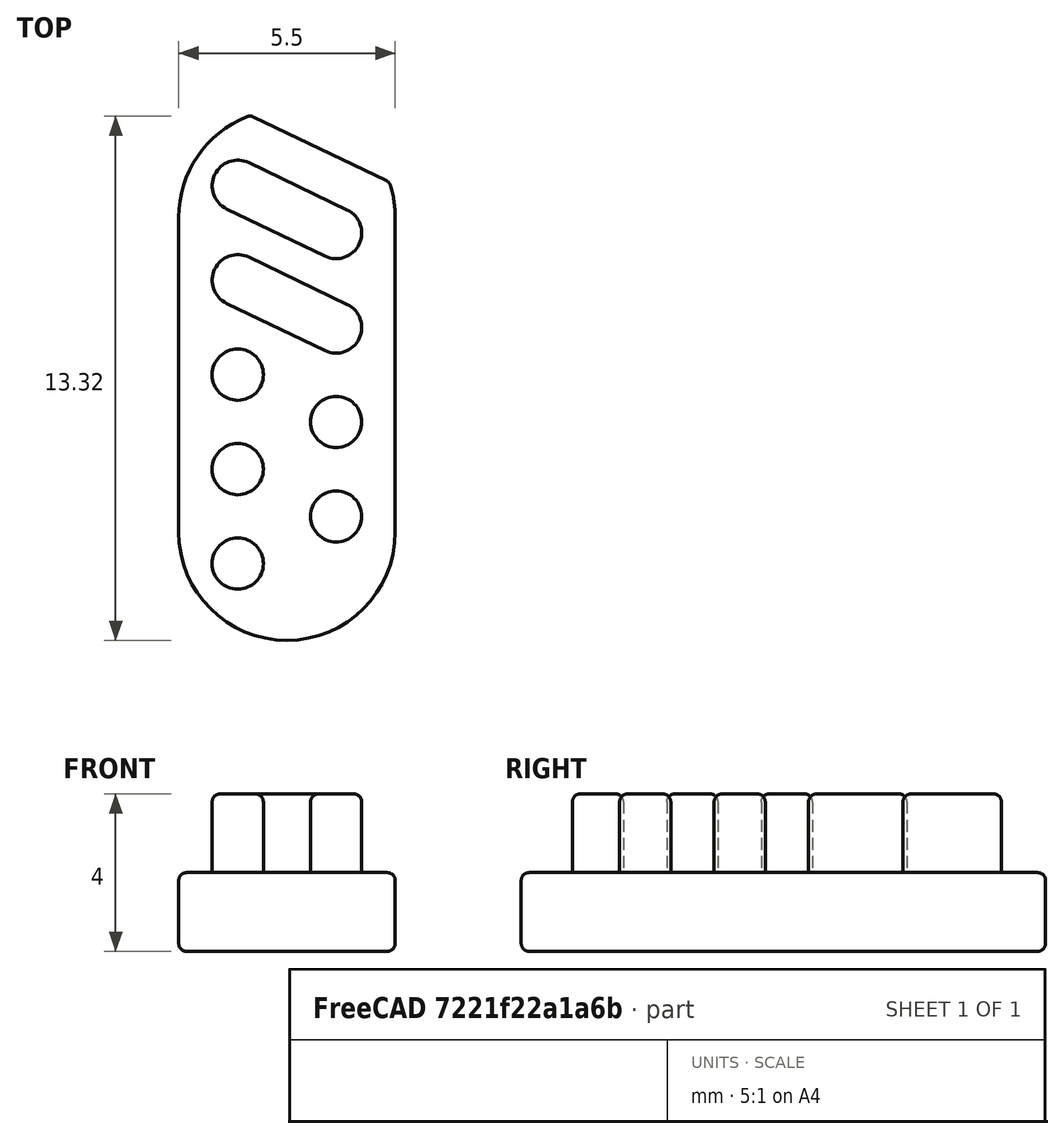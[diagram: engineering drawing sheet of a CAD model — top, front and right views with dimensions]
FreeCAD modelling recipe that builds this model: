
FCSTD DOCUMENT  (FreeCAD 0.18R13959 (Git))
Label: Light_Diffuser-PCB-v1.7
License: CreativeCommons Attribution-NonCommercial-ShareAlike
LicenseURL: http://creativecommons.org/licenses/by-nc-sa/4.0/
objects: Sketcher::SketchObject×3, PartDesign::Pad×2, PartDesign::Fillet×2, PartDesign::Body×1, Mesh::Feature×1
note: 10 computed .brp shape members not serialized (recipe doc carries the construction recipe); baked Part::Feature solids carry a one-line shape summary decoded from their .brp

FEATURE [Sketcher::SketchObject] Sketch
  MapMode = 5
  Support = -> [XY_Plane]
FEATURE [Sketcher::SketchObject] Sketch009
  MapMode = 5
  Placement = pos=(0,0,15.5) rot=(0,0,1;0rad)
  sketch-geometry (47):
    g0: LineSegment [constr] StartX=26.0494 StartY=8.19084 StartZ=0 EndX=28.5494 EndY=8.19084 EndZ=0
    g1: LineSegment [constr] StartX=28.5494 StartY=8.19084 StartZ=0 EndX=28.5494 EndY=-1.40916 EndZ=0
    g2: LineSegment [constr] StartX=28.5494 StartY=-1.40916 StartZ=0 EndX=26.0494 EndY=-1.40916 EndZ=0
    g3: LineSegment [constr] StartX=26.0494 StartY=-1.40916 StartZ=0 EndX=26.0494 EndY=8.19084 EndZ=0
    g4: LineSegment [constr] StartX=26.0494 StartY=6.99084 StartZ=0 EndX=28.5494 EndY=6.99084 EndZ=0
    g5: LineSegment [constr] StartX=26.0494 StartY=5.79084 StartZ=0 EndX=28.5494 EndY=5.79084 EndZ=0
    g6: LineSegment [constr] StartX=26.0494 StartY=4.59084 StartZ=0 EndX=28.5494 EndY=4.59084 EndZ=0
    g7: LineSegment [constr] StartX=26.0494 StartY=3.39084 StartZ=0 EndX=28.5494 EndY=3.39084 EndZ=0
    g8: LineSegment [constr] StartX=26.0494 StartY=2.19084 StartZ=0 EndX=28.5494 EndY=2.19084 EndZ=0
    g9: LineSegment [constr] StartX=26.0494 StartY=0.990836 StartZ=0 EndX=28.5494 EndY=0.990836 EndZ=0
    g10: LineSegment [constr] StartX=26.0494 StartY=-0.209164 StartZ=0 EndX=28.5494 EndY=-0.209164 EndZ=0
    g11: ArcOfCircle [constr] CenterX=26.0494 CenterY=8.19084 CenterZ=0 NormalX=0 NormalY=0 NormalZ=1 AngleXU=0 Radius=0.75 StartAngle=1.12328 EndAngle=4.26487
    g12: ArcOfCircle [constr] CenterX=28.5494 CenterY=6.99084 CenterZ=0 NormalX=0 NormalY=0 NormalZ=1 AngleXU=0 Radius=0.75 StartAngle=4.26487 EndAngle=7.40646
    g13: Circle [constr] CenterX=28.5494 CenterY=6.99084 CenterZ=0 NormalX=0 NormalY=0 NormalZ=1 AngleXU=0 Radius=0.75
    g14: Circle [constr] CenterX=26.0494 CenterY=8.19084 CenterZ=0 NormalX=0 NormalY=0 NormalZ=1 AngleXU=0 Radius=0.75
    g15: LineSegment [constr] StartX=25.5171 StartY=9.27827 StartZ=0 EndX=28.8383 EndY=7.68412 EndZ=0
    g16: LineSegment [constr] StartX=24.3258 StartY=8.18624 StartZ=0 EndX=27.642 EndY=6.59448 EndZ=0
    g17: LineSegment [constr] StartX=26.374 StartY=8.86698 StartZ=0 EndX=28.874 EndY=7.66698 EndZ=0
    g18: LineSegment [constr] StartX=25.7249 StartY=7.51469 StartZ=0 EndX=28.2249 EndY=6.31469 EndZ=0
    g19: ArcOfCircle [constr] CenterX=26.0494 CenterY=5.79084 CenterZ=0 NormalX=0 NormalY=0 NormalZ=1 AngleXU=0 Radius=0.75 StartAngle=1.34506 EndAngle=4.05341
    g20: LineSegment [constr] StartX=26.2173 StartY=6.52181 StartZ=0 EndX=28.7014 EndY=5.32527 EndZ=0
    g21: ArcOfCircle [constr] CenterX=28.5494 CenterY=4.59084 CenterZ=0 NormalX=0 NormalY=0 NormalZ=1 AngleXU=0 Radius=0.75 StartAngle=4.03537 EndAngle=7.64991
    g22: LineSegment [constr] StartX=25.5902 StartY=5.19787 StartZ=0 EndX=28.0796 EndY=4.00625 EndZ=0
    g23: Circle [constr] CenterX=26.0494 CenterY=-1.40916 CenterZ=0 NormalX=0 NormalY=0 NormalZ=1 AngleXU=0 Radius=0.75
    g24: Circle [constr] CenterX=28.5494 CenterY=-0.209164 CenterZ=0 NormalX=0 NormalY=0 NormalZ=1 AngleXU=0 Radius=0.75
    g25: Circle [constr] CenterX=26.0494 CenterY=0.990836 CenterZ=0 NormalX=0 NormalY=0 NormalZ=1 AngleXU=0 Radius=0.75
    g26: Circle [constr] CenterX=28.5494 CenterY=2.19084 CenterZ=0 NormalX=0 NormalY=0 NormalZ=1 AngleXU=0 Radius=0.75
    g27: Circle [constr] CenterX=26.0494 CenterY=3.39084 CenterZ=0 NormalX=0 NormalY=0 NormalZ=1 AngleXU=0 Radius=0.75
    g28: LineSegment [constr] StartX=25.99 StartY=-2.26963 StartZ=0 EndX=28.2803 EndY=-1.17028 EndZ=0
    g29: LineSegment [constr] StartX=24.2621 StartY=-1.43517 StartZ=0 EndX=27.5897 EndY=0.162095 EndZ=0
    g30: LineSegment [constr] StartX=24.4431 StartY=0.929921 StartZ=0 EndX=28.3215 EndY=-0.931678 EndZ=0
    g31: LineSegment [constr] StartX=25.7479 StartY=1.96747 StartZ=0 EndX=28.6552 EndY=0.57196 EndZ=0
    g32: LineSegment [constr] StartX=25.0985 StartY=-0.297502 StartZ=0 EndX=28.7983 EndY=1.4784 EndZ=0
    g33: LineSegment [constr] StartX=24.2499 StartY=0.959014 StartZ=0 EndX=27.3959 EndY=2.46909 EndZ=0
    g34: LineSegment [constr] StartX=24.4539 StartY=3.32474 StartZ=0 EndX=27.6201 EndY=1.80499 EndZ=0
    g35: Circle [constr] CenterX=26.0494 CenterY=2.19084 CenterZ=0 NormalX=0 NormalY=0 NormalZ=1 AngleXU=0 Radius=0.331828
    g36: Circle [constr] CenterX=28.5494 CenterY=0.990836 CenterZ=0 NormalX=0 NormalY=0 NormalZ=1 AngleXU=0 Radius=0.331828
    g37: Circle [constr] CenterX=26.0494 CenterY=-0.209164 CenterZ=0 NormalX=0 NormalY=0 NormalZ=1 AngleXU=0 Radius=0.331828
    g38: LineSegment [constr] StartX=27.2994 StartY=10.3721 StartZ=0 EndX=27.2994 EndY=-2.82328 EndZ=0
    g39: ArcOfCircle [constr] CenterX=27.2994 CenterY=7.39084 CenterZ=0 NormalX=0 NormalY=0 NormalZ=1 AngleXU=0 Radius=2.75 StartAngle=0 EndAngle=3.14159
    g40: ArcOfCircle CenterX=27.2994 CenterY=-0.609164 CenterZ=0 NormalX=0 NormalY=0 NormalZ=1 AngleXU=0 Radius=2.75 StartAngle=3.14159 EndAngle=6.28319
    g41: LineSegment StartX=24.5494 StartY=7.39084 StartZ=0 EndX=24.5494 EndY=-0.609164 EndZ=0
    g42: LineSegment StartX=30.0494 StartY=7.39084 StartZ=0 EndX=30.0494 EndY=-0.609164 EndZ=0
    g43: LineSegment [constr] StartX=24.5693 StartY=10.8425 StartZ=0 EndX=31.1469 EndY=7.68522 EndZ=0
    g44: ArcOfCircle CenterX=27.2994 CenterY=7.39084 CenterZ=0 NormalX=0 NormalY=0 NormalZ=1 AngleXU=0 Radius=2.75 StartAngle=1.91597 EndAngle=3.14159
    g45: ArcOfCircle CenterX=27.2994 CenterY=7.39084 CenterZ=0 NormalX=0 NormalY=0 NormalZ=1 AngleXU=0 Radius=2.75 StartAngle=0 EndAngle=0.330582
    g46: LineSegment StartX=26.3689 StartY=9.97863 StartZ=0 EndX=29.9005 EndY=8.28347 EndZ=0
  constraints (117):
    c: Coincident(g0,g1)
    c: Coincident(g1,g2)
    c: Coincident(g2,g3)
    c: Coincident(g3,g0)
    c: Horizontal(g0)
    c: Horizontal(g2)
    c: Vertical(g1)
    c: Vertical(g3)
    c: DistanceX(g0,g0) = 2.5
    c: DistanceY(g3,g3) = 9.6
    c: Horizontal(g4)
    c: Horizontal(g5)
    c: Horizontal(g6)
    c: Horizontal(g8)
    c: Horizontal(g9)
    c: DistanceY(g4,g0) = 1.2
    c: DistanceY(g5,g4) = 1.2
    c: DistanceY(g6,g5) = 1.2
    c: DistanceY(g7,g6) = 1.2
    c: DistanceY(g8,g7) = 1.2
    c: DistanceY(g9,g8) = 1.2
    c: Horizontal(g10)
    c: DistanceY(g10,g9) = 1.2
    c: PointOnObject(g4,g3)
    c: PointOnObject(g5,g3)
    c: PointOnObject(g6,g3)
    c: PointOnObject(g7,g3)
    c: PointOnObject(g8,g3)
    c: PointOnObject(g9,g3)
    c: PointOnObject(g10,g3)
    c: PointOnObject(g10,g1)
    c: PointOnObject(g9,g1)
    c: PointOnObject(g8,g1)
    c: PointOnObject(g7,g1)
    c: PointOnObject(g6,g1)
    c: PointOnObject(g5,g1)
    c: PointOnObject(g4,g1)
    c: Coincident(g11,g0)
    c: Coincident(g12,g4)
    c: Radius(g11) = 0.75
    c: Radius(g12) = 0.75
    c: Coincident(g13,g4)
    c: Coincident(g14,g0)
    c: Radius(g14) = 0.75
    c: Radius(g13) = 0.75
    c: Tangent(g15,g13)
    c: Tangent(g15,g14)
    c: Tangent(g16,g14)
    c: Tangent(g16,g13)
    c: PointOnObject(g17,g15)
    c: PointOnObject(g17,g15)
    c: PointOnObject(g18,g16)
    c: PointOnObject(g18,g16)
    c: Coincident(g17,g11)
    c: Coincident(g11,g18)
    c: Coincident(g17,g12)
    c: Coincident(g12,g18)
    c: Equal(g11,g19) = 0.75
    c: Equal(g12,g21) = 0.75
    c: Coincident(g20,g19)
    c: Coincident(g19,g22)
    c: Coincident(g20,g21)
    c: Coincident(g21,g22)
    c: Coincident(g19,g5)
    c: Coincident(g21,g6)
    c: Coincident(g24,g10)
    c: Coincident(g25,g9)
    c: Coincident(g26,g8)
    c: Coincident(g27,g7)
    c: Radius(g27) = 0.75
    c: Radius(g26) = 0.75
    c: Radius(g25) = 0.75
    c: Radius(g24) = 0.75
    c: Radius(g23) = 0.75
    c: Tangent(g31,g24)
    c: Tangent(g31,g25)
    c: Tangent(g30,g25)
    c: Tangent(g30,g24)
    c: Tangent(g29,g23)
    c: Tangent(g29,g24)
    c: Coincident(g23,g2)
    c: Tangent(g23,g28)
    c: Tangent(g28,g24)
    c: Tangent(g32,g25)
    c: Tangent(g32,g26)
    c: Tangent(g33,g26)
    c: Tangent(g33,g25)
    c: Tangent(g34,g27)
    c: Tangent(g34,g26)
    c: Coincident(g35,g8)
    c: Tangent(g35,g34)
    c: Coincident(g36,g9)
    c: Tangent(g36,g32)
    c: Coincident(g37,g10)
    c: Tangent(g37,g30)
    c: Vertical(g38)
    c: Symmetric(g0,g0,g38)
    c: Tangent(g39,g42)
    c: Tangent(g39,g41)
    c: Tangent(g41,g40)
    c: Tangent(g42,g40)
    c: Vertical(g41)
    c: Equal(g39,g40)
    c: PointOnObject(g39,g38)
    c: DistanceY(g40,g39) = 8
    c: Symmetric(g40,g39,g7)
    c: DistanceX(g40,g40) = 5.5
    c: Parallel(g43,g15)
    c: Coincident(g44,g39)
    c: Coincident(g44,g39)
    c: Coincident(g45,g39)
    c: Coincident(g45,g39)
    c: Distance(g15,g43) = 1
    c: PointOnObject(g46,g43)
    c: PointOnObject(g46,g43)
    c: Coincident(g45,g46)
    c: Coincident(g44,g46)
FEATURE [PartDesign::Pad] Pad
  Length = 2
  Length2 = 100
  Placement = pos=(0,0,15.5) rot=(0,0,1;0rad)
  Profile = -> Sketch009
  Type = 0
FEATURE [Sketcher::SketchObject] Sketch010
  ExternalGeometry = -> [Pad]
  MapMode = 5
  Placement = pos=(0,0,17.5) rot=(0,0,1;0rad)
  Support = -> [Pad]
  expr: Constraints[39] = Sketch009.Constraints[43]
  expr: Constraints[8] = Sketch009.Constraints[8]
  expr: Constraints[40] = Sketch009.Constraints[44]
  expr: Constraints[56] = Sketch009.Constraints[72]
  expr: Constraints[57] = Sketch009.Constraints[73]
  expr: Constraints[15] = Sketch009.Constraints[15]
  expr: Constraints[55] = Sketch009.Constraints[71]
  expr: Constraints[53] = Sketch009.Constraints[69]
  expr: Constraints[9] = Sketch009.Constraints[9]
  expr: Constraints[54] = Sketch009.Constraints[70]
  expr: Constraints[17] = Sketch009.Constraints[17]
  expr: Constraints[19] = Sketch009.Constraints[19]
  expr: Constraints[18] = Sketch009.Constraints[18]
  expr: Constraints[16] = Sketch009.Constraints[16]
  expr: Constraints[20] = Sketch009.Constraints[20]
  expr: Constraints[22] = Sketch009.Constraints[22]
  sketch-geometry (60):
    g0: LineSegment [constr] StartX=26.0494 StartY=8.19084 StartZ=0 EndX=28.5494 EndY=8.19084 EndZ=0
    g1: LineSegment [constr] StartX=28.5494 StartY=8.19084 StartZ=0 EndX=28.5494 EndY=-1.40916 EndZ=0
    g2: LineSegment [constr] StartX=28.5494 StartY=-1.40916 StartZ=0 EndX=26.0494 EndY=-1.40916 EndZ=0
    g3: LineSegment [constr] StartX=26.0494 StartY=-1.40916 StartZ=0 EndX=26.0494 EndY=8.19084 EndZ=0
    g4: LineSegment [constr] StartX=26.0494 StartY=6.99084 StartZ=0 EndX=28.5494 EndY=6.99084 EndZ=0
    g5: LineSegment [constr] StartX=26.0494 StartY=5.79084 StartZ=0 EndX=28.5494 EndY=5.79084 EndZ=0
    g6: LineSegment [constr] StartX=26.0494 StartY=4.59084 StartZ=0 EndX=28.5494 EndY=4.59084 EndZ=0
    g7: LineSegment [constr] StartX=26.0494 StartY=3.39084 StartZ=0 EndX=28.5494 EndY=3.39084 EndZ=0
    g8: LineSegment [constr] StartX=26.0494 StartY=2.19084 StartZ=0 EndX=28.5494 EndY=2.19084 EndZ=0
    g9: LineSegment [constr] StartX=26.0494 StartY=0.990836 StartZ=0 EndX=28.5494 EndY=0.990836 EndZ=0
    g10: LineSegment [constr] StartX=26.0494 StartY=-0.209164 StartZ=0 EndX=28.5494 EndY=-0.209164 EndZ=0
    g11: Circle [constr] CenterX=28.5494 CenterY=6.99084 CenterZ=0 NormalX=0 NormalY=0 NormalZ=1 AngleXU=0 Radius=0.75
    g12: Circle [constr] CenterX=26.0494 CenterY=8.19084 CenterZ=0 NormalX=0 NormalY=0 NormalZ=1 AngleXU=0 Radius=0.75
    g13: LineSegment [constr] StartX=25.5635 StartY=9.25599 StartZ=0 EndX=28.8763 EndY=7.66586 EndZ=0
    g14: LineSegment [constr] StartX=24.3756 StartY=8.16234 StartZ=0 EndX=27.694 EndY=6.56949 EndZ=0
    g15: LineSegment [constr] StartX=25.798 StartY=9.14342 StartZ=0 EndX=28.298 EndY=7.94342 EndZ=0
    g16: LineSegment [constr] StartX=25.1489 StartY=7.79113 StartZ=0 EndX=27.6489 EndY=6.59113 EndZ=0
    g17: Circle [constr] CenterX=26.0494 CenterY=-1.40916 CenterZ=0 NormalX=0 NormalY=0 NormalZ=1 AngleXU=0 Radius=0.75
    g18: Circle [constr] CenterX=28.5494 CenterY=-0.209164 CenterZ=0 NormalX=0 NormalY=0 NormalZ=1 AngleXU=0 Radius=0.75
    g19: Circle [constr] CenterX=26.0494 CenterY=0.990836 CenterZ=0 NormalX=0 NormalY=0 NormalZ=1 AngleXU=0 Radius=0.75
    g20: Circle [constr] CenterX=28.5494 CenterY=2.19084 CenterZ=0 NormalX=0 NormalY=0 NormalZ=1 AngleXU=0 Radius=0.75
    g21: Circle [constr] CenterX=26.0494 CenterY=3.39084 CenterZ=0 NormalX=0 NormalY=0 NormalZ=1 AngleXU=0 Radius=0.75
    g22: LineSegment [constr] StartX=26.1522 StartY=-2.19175 StartZ=0 EndX=28.4416 EndY=-1.09284 EndZ=0
    g23: LineSegment [constr] StartX=24.424 StartY=-1.35742 StartZ=0 EndX=27.7513 EndY=0.239661 EndZ=0
    g24: LineSegment [constr] StartX=24.4948 StartY=0.905132 StartZ=0 EndX=28.3731 EndY=-0.956467 EndZ=0
    g25: LineSegment [constr] StartX=25.7996 StartY=1.94268 StartZ=0 EndX=28.7069 EndY=0.54717 EndZ=0
    g26: LineSegment [constr] StartX=25.26 StartY=-0.220018 StartZ=0 EndX=28.9598 EndY=1.55589 EndZ=0
    g27: LineSegment [constr] StartX=24.4114 StartY=1.0365 StartZ=0 EndX=27.5573 EndY=2.54657 EndZ=0
    g28: LineSegment [constr] StartX=24.5064 StartY=3.29957 StartZ=0 EndX=27.6722 EndY=1.77997 EndZ=0
    g29: Circle [constr] CenterX=26.0494 CenterY=2.19084 CenterZ=0 NormalX=0 NormalY=0 NormalZ=1 AngleXU=0 Radius=0.331828
    g30: Circle [constr] CenterX=28.5494 CenterY=0.990836 CenterZ=0 NormalX=0 NormalY=0 NormalZ=1 AngleXU=0 Radius=0.331828
    g31: Circle [constr] CenterX=26.0494 CenterY=-0.209164 CenterZ=0 NormalX=0 NormalY=0 NormalZ=1 AngleXU=0 Radius=0.331828
    g32: LineSegment [constr] StartX=27.2994 StartY=10.5023 StartZ=0 EndX=27.2994 EndY=-2.69309 EndZ=0
    g33: Circle [constr] CenterX=26.0494 CenterY=5.79084 CenterZ=0 NormalX=0 NormalY=0 NormalZ=1 AngleXU=0 Radius=0.75
    g34: Circle [constr] CenterX=28.5494 CenterY=4.59084 CenterZ=0 NormalX=0 NormalY=0 NormalZ=1 AngleXU=0 Radius=0.75
    g35: LineSegment [constr] StartX=25.2568 StartY=7.00319 StartZ=0 EndX=29.1124 EndY=5.15253 EndZ=0
    g36: LineSegment [constr] StartX=24.5022 StartY=5.70156 StartZ=0 EndX=28.1414 EndY=3.95476 EndZ=0
    g37: Circle CenterX=26.0494 CenterY=3.39084 CenterZ=0 NormalX=0 NormalY=0 NormalZ=1 AngleXU=0 Radius=0.65
    g38: Circle CenterX=28.5494 CenterY=2.19084 CenterZ=0 NormalX=0 NormalY=0 NormalZ=1 AngleXU=0 Radius=0.65
    g39: Circle CenterX=26.0494 CenterY=0.990836 CenterZ=0 NormalX=0 NormalY=0 NormalZ=1 AngleXU=0 Radius=0.65
    g40: Circle CenterX=26.0494 CenterY=-1.40916 CenterZ=0 NormalX=0 NormalY=0 NormalZ=1 AngleXU=0 Radius=0.65
    g41: Circle CenterX=28.5494 CenterY=-0.209164 CenterZ=0 NormalX=0 NormalY=0 NormalZ=1 AngleXU=0 Radius=0.65
    g42: Circle [constr] CenterX=28.5494 CenterY=6.99084 CenterZ=0 NormalX=0 NormalY=0 NormalZ=1 AngleXU=0 Radius=0.65
    g43: Circle [constr] CenterX=26.0494 CenterY=8.19084 CenterZ=0 NormalX=0 NormalY=0 NormalZ=1 AngleXU=0 Radius=0.65
    g44: LineSegment [constr] StartX=25.0896 StartY=9.37255 StartZ=0 EndX=28.8024 EndY=7.59041 EndZ=0
    g45: LineSegment [constr] StartX=24.3536 StartY=8.28381 StartZ=0 EndX=28.1684 EndY=6.45273 EndZ=0
    g46: Circle [constr] CenterX=26.0494 CenterY=5.79084 CenterZ=0 NormalX=0 NormalY=0 NormalZ=1 AngleXU=0 Radius=0.65
    g47: Circle [constr] CenterX=28.5494 CenterY=4.59084 CenterZ=0 NormalX=0 NormalY=0 NormalZ=1 AngleXU=0 Radius=0.65
    g48: LineSegment [constr] StartX=24.9879 StartY=7.02135 StartZ=0 EndX=28.8106 EndY=5.18647 EndZ=0
    g49: LineSegment [constr] StartX=24.6124 StartY=5.75959 StartZ=0 EndX=28.3692 EndY=3.95636 EndZ=0
    g50: ArcOfCircle CenterX=26.0494 CenterY=8.19084 CenterZ=0 NormalX=0 NormalY=0 NormalZ=1 AngleXU=0 Radius=0.65 StartAngle=1.12328 EndAngle=4.26488
    g51: ArcOfCircle CenterX=28.5494 CenterY=6.99084 CenterZ=0 NormalX=0 NormalY=0 NormalZ=1 AngleXU=0 Radius=0.65 StartAngle=4.26487 EndAngle=7.40646
    g52: ArcOfCircle CenterX=26.0494 CenterY=5.79084 CenterZ=0 NormalX=0 NormalY=0 NormalZ=1 AngleXU=0 Radius=0.65 StartAngle=1.12328 EndAngle=4.26487
    g53: ArcOfCircle CenterX=28.5494 CenterY=4.59084 CenterZ=0 NormalX=0 NormalY=0 NormalZ=1 AngleXU=0 Radius=0.65 StartAngle=4.26488 EndAngle=7.40646
    g54: LineSegment StartX=26.3307 StartY=8.77683 StartZ=0 EndX=28.8307 EndY=7.57683 EndZ=0
    g55: LineSegment StartX=25.7681 StartY=7.60484 StartZ=0 EndX=28.2681 EndY=6.40485 EndZ=0
    g56: LineSegment StartX=26.3307 StartY=6.37683 StartZ=0 EndX=28.8307 EndY=5.17683 EndZ=0
    g57: LineSegment StartX=25.7681 StartY=5.20485 StartZ=0 EndX=28.2681 EndY=4.00484 EndZ=0
    g58: LineSegment [constr] StartX=24.5494 StartY=7.20634 StartZ=0 EndX=24.5494 EndY=-0.230688 EndZ=0
    g59: LineSegment [constr] StartX=30.0494 StartY=7.20634 StartZ=0 EndX=30.0494 EndY=0.145812 EndZ=0
  constraints (146):
    c: Coincident(g0,g1)
    c: Coincident(g1,g2)
    c: Coincident(g2,g3)
    c: Coincident(g3,g0)
    c: Horizontal(g0)
    c: Horizontal(g2)
    c: Vertical(g1)
    c: Vertical(g3)
    c: DistanceX(g0,g0) = 2.5
    c: DistanceY(g3,g3) = 9.6
    c: Horizontal(g4)
    c: Horizontal(g5)
    c: Horizontal(g6)
    c: Horizontal(g8)
    c: Horizontal(g9)
    c: DistanceY(g4,g0) = 1.2
    c: DistanceY(g5,g4) = 1.2
    c: DistanceY(g6,g5) = 1.2
    c: DistanceY(g7,g6) = 1.2
    c: DistanceY(g8,g7) = 1.2
    c: DistanceY(g9,g8) = 1.2
    c: Horizontal(g10)
    c: DistanceY(g10,g9) = 1.2
    c: PointOnObject(g4,g3)
    c: PointOnObject(g5,g3)
    c: PointOnObject(g6,g3)
    c: PointOnObject(g7,g3)
    c: PointOnObject(g8,g3)
    c: PointOnObject(g9,g3)
    c: PointOnObject(g10,g3)
    c: PointOnObject(g10,g1)
    c: PointOnObject(g9,g1)
    c: PointOnObject(g8,g1)
    c: PointOnObject(g7,g1)
    c: PointOnObject(g6,g1)
    c: PointOnObject(g5,g1)
    c: PointOnObject(g4,g1)
    c: Coincident(g11,g4)
    c: Coincident(g12,g0)
    c: Radius(g12) = 0.75
    c: Radius(g11) = 0.75
    c: Tangent(g13,g11)
    c: Tangent(g13,g12)
    c: Tangent(g14,g12)
    c: Tangent(g14,g11)
    c: PointOnObject(g15,g13)
    c: PointOnObject(g15,g13)
    c: PointOnObject(g16,g14)
    c: PointOnObject(g16,g14)
    c: Coincident(g18,g10)
    c: Coincident(g19,g9)
    c: Coincident(g20,g8)
    c: Coincident(g21,g7)
    c: Radius(g21) = 0.75
    c: Radius(g20) = 0.75
    c: Radius(g19) = 0.75
    c: Radius(g18) = 0.75
    c: Radius(g17) = 0.75
    c: Tangent(g25,g18)
    c: Tangent(g25,g19)
    c: Tangent(g24,g19)
    c: Tangent(g24,g18)
    c: Tangent(g23,g17)
    c: Tangent(g23,g18)
    c: Coincident(g17,g2)
    c: Tangent(g17,g22)
    c: Tangent(g22,g18)
    c: Tangent(g26,g19)
    c: Tangent(g26,g20)
    c: Tangent(g27,g20)
    c: Tangent(g27,g19)
    c: Tangent(g28,g21)
    c: Tangent(g28,g20)
    c: Coincident(g29,g8)
    c: Tangent(g29,g28)
    c: Coincident(g30,g9)
    c: Tangent(g30,g26)
    c: Coincident(g31,g10)
    c: Tangent(g31,g24)
    c: Vertical(g32)
    c: Symmetric(g0,g0,g32)
    c: Coincident(g33,g5)
    c: Radius(g33) = 0.75
    c: Coincident(g34,g6)
    c: Radius(g34) = 0.75
    c: Tangent(g33,g35)
    c: Tangent(g35,g34)
    c: Tangent(g36,g33)
    c: Tangent(g36,g34)
    c: Coincident(g37,g7)
    c: Radius(g37) = 0.65
    c: Coincident(g38,g8)
    c: Coincident(g39,g9)
    c: Coincident(g40,g2)
    c: Radius(g38) = 0.65
    c: Radius(g39) = 0.65
    c: Coincident(g41,g10)
    c: Radius(g41) = 0.65
    c: Radius(g40) = 0.65
    c: Coincident(g42,g4)
    c: Radius(g42) = 0.65
    c: Coincident(g43,g0)
    c: Radius(g43) = 0.65
    c: Tangent(g44,g42)
    c: Tangent(g44,g43)
    c: Tangent(g45,g43)
    c: Tangent(g45,g42)
    c: Coincident(g46,g5)
    c: Coincident(g47,g6)
    c: Radius(g47) = 0.65
    c: Radius(g46) = 0.65
    c: Tangent(g48,g47)
    c: Tangent(g48,g46)
    c: Tangent(g49,g47)
    c: Tangent(g49,g46)
    c: Coincident(g50,g0)
    c: PointOnObject(g50,g43)
    c: Coincident(g51,g4)
    c: PointOnObject(g51,g42)
    c: Coincident(g52,g5)
    c: PointOnObject(g52,g46)
    c: Coincident(g53,g6)
    c: PointOnObject(g53,g47)
    c: PointOnObject(g54,g44)
    c: PointOnObject(g54,g44)
    c: PointOnObject(g55,g45)
    c: PointOnObject(g55,g45)
    c: PointOnObject(g56,g48)
    c: PointOnObject(g56,g48)
    c: PointOnObject(g57,g49)
    c: PointOnObject(g57,g49)
    c: Coincident(g54,g50)
    c: Coincident(g54,g51)
    c: Coincident(g51,g55)
    c: Coincident(g55,g50)
    c: Coincident(g56,g52)
    c: Coincident(g56,g53)
    c: Coincident(g52,g57)
    c: Coincident(g57,g53)
    c: PointOnObject(g58,g-4)
    c: PointOnObject(g58,g-4)
    c: PointOnObject(g59,g-3)
    c: PointOnObject(g59,g-3)
    c: Symmetric(g58,g59,g32)
    c: Horizontal(g7)
    c: Symmetric(g-4,g-4,g7)
FEATURE [PartDesign::Pad] Pad001
  BaseFeature = -> Pad
  Length = 2
  Length2 = 100
  Placement = pos=(0,0,15.5) rot=(0,0,1;0rad)
  Profile = -> Sketch010
  Type = 0
FEATURE [PartDesign::Fillet] Fillet
  Base = -> Pad001 [Edge45,Edge51,Edge49,Edge37,Edge57,Edge53,Edge55]
  BaseFeature = -> Pad001
  Placement = pos=(0,0,15.5) rot=(0,0,1;0rad)
  Radius = 0.2
FEATURE [PartDesign::Fillet] Fillet001
  Base = -> Fillet [Edge13,Edge40,Edge47,Edge16,Edge43,Edge45]
  BaseFeature = -> Fillet
  Placement = pos=(0,0,15.5) rot=(0,0,1;0rad)
  Radius = 0.2
FEATURE [PartDesign::Body] Body
  Group = -> [Sketch,Sketch009,Pad,Sketch010,Pad001,Fillet,Fillet001]
  Origin = -> Origin
  Tip = -> Fillet001
FEATURE [Mesh::Feature] Mesh  label="Fillet001 (Meshed)"
